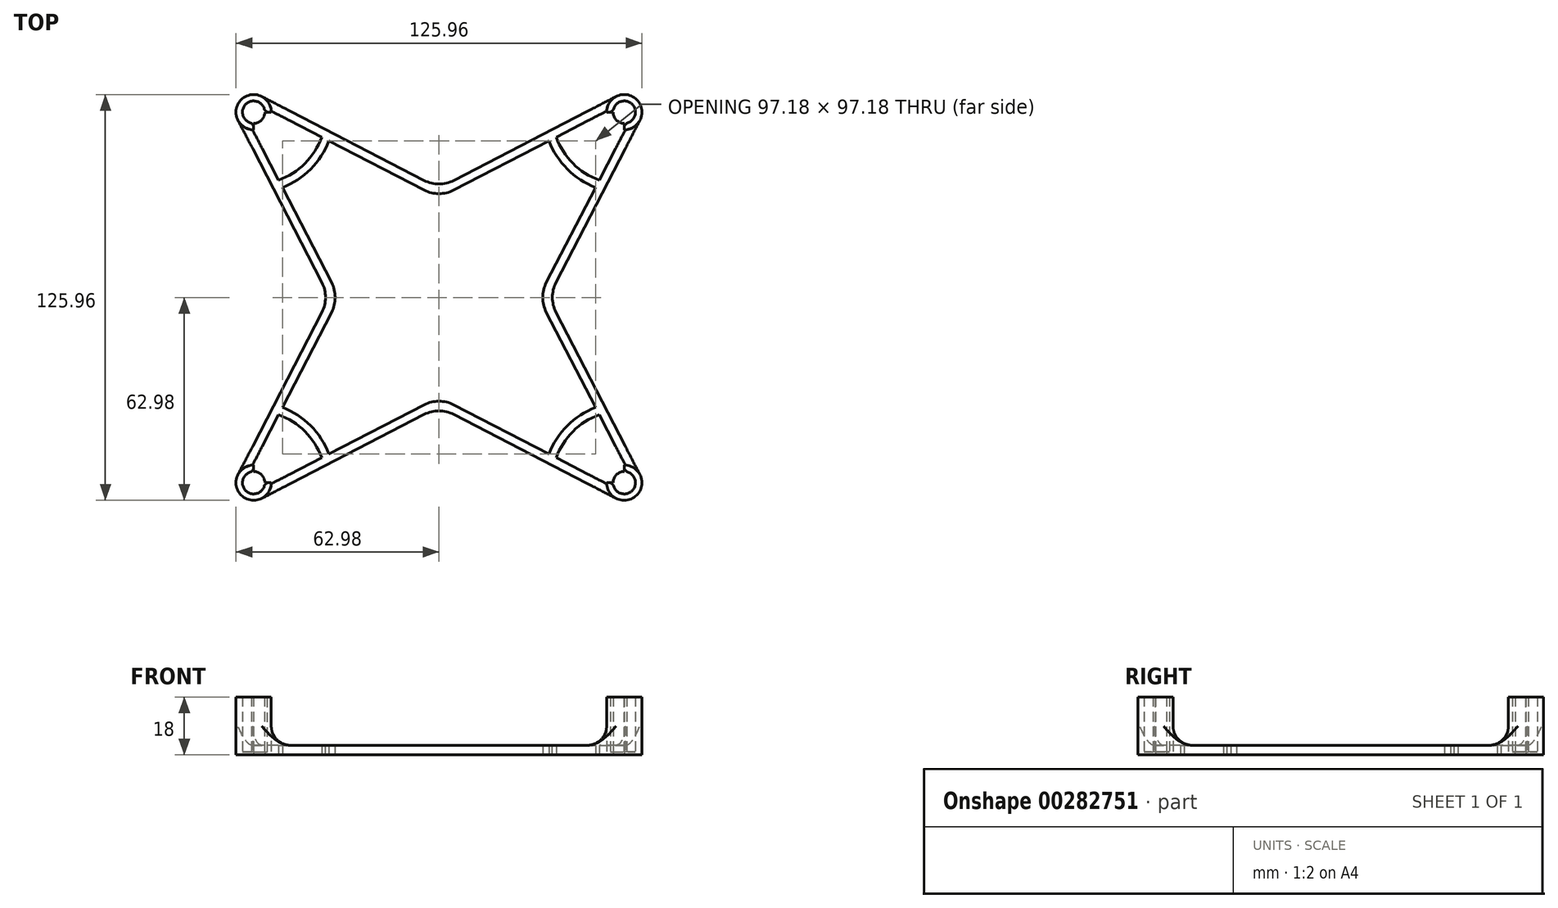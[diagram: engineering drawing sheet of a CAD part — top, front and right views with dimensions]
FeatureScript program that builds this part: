
annotation { "Feature Type Name" : "Feature", "Feature Type Description" : "" }
export const myFeature = defineFeature(function(context is Context, id is Id, definition is map)
    precondition{}
    {
        {
            var Q0;
            Q0=qCreatedBy(makeId("Top.planeOp"),FACE);
            var sketch = newSketch(context, id + "F0", { "sketchPlane" : qUnion([Q0])});
            skLineSegment(sketch, "E0.rect.bottom", {"start": v(57.5, 57.5) * mm, "end": v(-57.5, 57.5) * mm});
            skLineSegment(sketch, "E0.rect.top", {"start": v(57.5, -57.5) * mm, "end": v(-57.5, -57.5) * mm});
            skLineSegment(sketch, "E0.rect.left", {"start": v(57.5, 57.5) * mm, "end": v(57.5, -57.5) * mm});
            skLineSegment(sketch, "E0.rect.right", {"start": v(-57.5, 57.5) * mm, "end": v(-57.5, -57.5) * mm});
            skPoint(sketch, "E0.rect.middle", {"position": v(0, 0) * mm});
            skLineSegment(sketch, "E1", {"start": v(0, 33.94) * mm, "end": v(-33.94, 0) * mm});
            skLineSegment(sketch, "E2", {"start": v(-33.94, 0) * mm, "end": v(0, -33.94) * mm});
            skLineSegment(sketch, "E3", {"start": v(0, -33.94) * mm, "end": v(33.94, 0) * mm});
            skLineSegment(sketch, "E4", {"start": v(33.94, 0) * mm, "end": v(0, 33.94) * mm});
            skCircle(sketch, "E5", {"center": v(57.5, 57.5) * mm, "radius": 3.48 * mm});
            skCircle(sketch, "E6", {"center": v(57.5, 57.5) * mm, "radius": 5.47 * mm});
            skLineSegment(sketch, "E7", {"start": v(57.5, 60.98) * mm, "end": v(57.5, 62.98) * mm, "construction": true});
            skCircle(sketch, "E8", {"center": v(-57.5, 57.5) * mm, "radius": 3.48 * mm});
            skCircle(sketch, "E9", {"center": v(-57.5, 57.5) * mm, "radius": 5.47 * mm});
            skCircle(sketch, "E10", {"center": v(-57.5, -57.5) * mm, "radius": 3.48 * mm});
            skCircle(sketch, "E11", {"center": v(-57.5, -57.5) * mm, "radius": 5.47 * mm});
            skCircle(sketch, "E12", {"center": v(57.5, -57.5) * mm, "radius": 3.48 * mm});
            skCircle(sketch, "E13", {"center": v(57.5, -57.5) * mm, "radius": 5.47 * mm});
            skLineSegment(sketch, "E14", {"start": v(62.36, 54.99) * mm, "end": v(33.94, 0) * mm});
            skLineSegment(sketch, "E15", {"start": v(33.94, 0) * mm, "end": v(62.36, -54.99) * mm});
            skLineSegment(sketch, "E16", {"start": v(54.99, -62.36) * mm, "end": v(0, -33.94) * mm});
            skLineSegment(sketch, "E17", {"start": v(0, -33.94) * mm, "end": v(-54.99, -62.36) * mm});
            skLineSegment(sketch, "E18", {"start": v(-62.36, -54.99) * mm, "end": v(-33.94, 0) * mm});
            skLineSegment(sketch, "E19", {"start": v(-33.94, 0) * mm, "end": v(-62.36, 54.99) * mm});
            skLineSegment(sketch, "E20", {"start": v(-54.99, 62.36) * mm, "end": v(0, 33.94) * mm});
            skLineSegment(sketch, "E21", {"start": v(0, 33.94) * mm, "end": v(54.99, 62.36) * mm});
            skLineSegment(sketch, "E22.0", {"start": v(30.94, 0) * mm, "end": v(0, 30.94) * mm});
            skLineSegment(sketch, "E22.1", {"start": v(0, -30.94) * mm, "end": v(30.94, 0) * mm});
            skLineSegment(sketch, "E22.2", {"start": v(-30.94, 0) * mm, "end": v(0, -30.94) * mm});
            skLineSegment(sketch, "E22.3", {"start": v(0, 30.94) * mm, "end": v(-30.94, 0) * mm});
            skLineSegment(sketch, "E23", {"start": v(-30.94, 0) * mm, "end": v(-57.84, 52.04) * mm});
            skLineSegment(sketch, "E24", {"start": v(-30.94, 0) * mm, "end": v(-57.84, -52.04) * mm});
            skLineSegment(sketch, "E25", {"start": v(30.94, 0) * mm, "end": v(33.94, 0) * mm, "construction": true});
            skLineSegment(sketch, "E26", {"start": v(0, -30.94) * mm, "end": v(-52.04, -57.84) * mm});
            skLineSegment(sketch, "E27", {"start": v(0, -30.94) * mm, "end": v(52.04, -57.84) * mm});
            skLineSegment(sketch, "E28", {"start": v(57.84, -52.04) * mm, "end": v(30.94, 0) * mm});
            skLineSegment(sketch, "E29", {"start": v(30.94, 0) * mm, "end": v(57.84, 52.04) * mm});
            skLineSegment(sketch, "E30", {"start": v(52.04, 57.84) * mm, "end": v(0, 30.94) * mm});
            skLineSegment(sketch, "E31", {"start": v(0, 30.94) * mm, "end": v(-52.04, 57.84) * mm});
            skCircle(sketch, "E32", {"center": v(57.5, 57.5) * mm, "radius": 22.5 * mm});
            skCircle(sketch, "E33", {"center": v(57.5, 57.5) * mm, "radius": 25 * mm});
            skLineSegment(sketch, "E34", {"start": v(57.5, 80) * mm, "end": v(57.5, 82.5) * mm, "construction": true});
            skCircle(sketch, "E35", {"center": v(-57.5, 57.5) * mm, "radius": 22.5 * mm});
            skCircle(sketch, "E36", {"center": v(-57.5, 57.5) * mm, "radius": 25 * mm});
            skCircle(sketch, "E37", {"center": v(-57.5, -57.5) * mm, "radius": 22.5 * mm});
            skCircle(sketch, "E38", {"center": v(-57.5, -57.5) * mm, "radius": 25 * mm});
            skCircle(sketch, "E39", {"center": v(57.5, -57.5) * mm, "radius": 22.5 * mm});
            skCircle(sketch, "E40", {"center": v(57.5, -57.5) * mm, "radius": 25 * mm});
            skSolve(sketch);
        }
        {
            var Q0;
            {var subQ1=sQuery(id+"F0.wireOp",EDGE,"E23");var subQ5=sQuery(id+"F0.wireOp",EDGE,"E0.rect.right");var subQ6=makeQuery(id+"F0.imprint","INTERSECT",VERTEX,{"derivedFrom":[subQ5,subQ1]});Q0=makeQuery(id+"F0.imprint","IMPRINT",FACE,{"disambiguationData":[TD([[makeQuery(id+"F0.imprint","IMPRINT",EDGE,{"disambiguationData":[TD([[subQ6,-1.0]])],"derivedFrom":subQ5}),1.0]])]});}
            var Q1;
            {var subQ1=sQuery(id+"F0.wireOp",EDGE,"E0.rect.right");var subQ5=sQuery(id+"F0.wireOp",EDGE,"E23");var subQ6=makeQuery(id+"F0.imprint","INTERSECT",VERTEX,{"derivedFrom":[subQ1,subQ5]});Q1=makeQuery(id+"F0.imprint","IMPRINT",FACE,{"disambiguationData":[TD([[makeQuery(id+"F0.imprint","IMPRINT",EDGE,{"disambiguationData":[TD([[subQ6,-1.0]])],"derivedFrom":subQ1}),-1.0]])]});}
            var Q2;
            {var subQ0=sQuery(id+"F0.wireOp",EDGE,"E9");var subQ7=sQuery(id+"F0.wireOp",EDGE,"E0.rect.bottom");var subQ8=makeQuery(id+"F0.imprint","INTERSECT",VERTEX,{"derivedFrom":[subQ7,subQ0]});Q2=makeQuery(id+"F0.imprint","IMPRINT",FACE,{"disambiguationData":[TD([[makeQuery(id+"F0.imprint","IMPRINT",EDGE,{"disambiguationData":[TD([[subQ8,-1.0]])],"derivedFrom":subQ7}),-1.0]])]});}
            var Q3;
            {var subQ1=sQuery(id+"F0.wireOp",EDGE,"E0.rect.bottom");var subQ5=sQuery(id+"F0.wireOp",EDGE,"E20");var subQ6=makeQuery(id+"F0.imprint","INTERSECT",VERTEX,{"derivedFrom":[subQ1,subQ5]});Q3=makeQuery(id+"F0.imprint","IMPRINT",FACE,{"disambiguationData":[TD([[makeQuery(id+"F0.imprint","IMPRINT",EDGE,{"disambiguationData":[TD([[subQ6,-1.0]])],"derivedFrom":subQ1}),-1.0]])]});}
            var Q4;
            {var subQ3=sQuery(id+"F0.wireOp",EDGE,"E20");var subQ5=sQuery(id+"F0.wireOp",EDGE,"E0.rect.bottom");var subQ7=makeQuery(id+"F0.imprint","INTERSECT",VERTEX,{"derivedFrom":[subQ5,subQ3]});Q4=makeQuery(id+"F0.imprint","IMPRINT",FACE,{"disambiguationData":[TD([[makeQuery(id+"F0.imprint","IMPRINT",EDGE,{"disambiguationData":[TD([[subQ7,-1.0]])],"derivedFrom":subQ5}),1.0]])]});}
            var Q5;
            {var subQ0=sQuery(id+"F0.wireOp",EDGE,"E36");var subQ3=sQuery(id+"F0.wireOp",EDGE,"E19");var subQ4=makeQuery(id+"F0.imprint","INTERSECT",VERTEX,{"derivedFrom":[subQ3,subQ0]});Q5=makeQuery(id+"F0.imprint","IMPRINT",FACE,{"disambiguationData":[TD([[makeQuery(id+"F0.imprint","IMPRINT",EDGE,{"disambiguationData":[TD([[subQ4,-1.0]])],"derivedFrom":subQ3}),-1.0]])]});}
            var Q6;
            {var subQ1=sQuery(id+"F0.wireOp",EDGE,"E23");var subQ5=sQuery(id+"F0.wireOp",EDGE,"E1");var subQ6=makeQuery(id+"F0.imprint","INTERSECT",VERTEX,{"derivedFrom":[subQ5,subQ1]});Q6=makeQuery(id+"F0.imprint","IMPRINT",FACE,{"disambiguationData":[TD([[makeQuery(id+"F0.imprint","IMPRINT",EDGE,{"disambiguationData":[TD([[subQ6,-1.0]])],"derivedFrom":subQ1}),1.0]])]});}
            var Q7;
            {var subQ3=sQuery(id+"F0.wireOp",EDGE,"E20");var subQ5=sQuery(id+"F0.wireOp",EDGE,"E35");var subQ7=makeQuery(id+"F0.imprint","INTERSECT",VERTEX,{"derivedFrom":[subQ3,subQ5]});Q7=makeQuery(id+"F0.imprint","IMPRINT",FACE,{"disambiguationData":[TD([[makeQuery(id+"F0.imprint","IMPRINT",EDGE,{"disambiguationData":[TD([[subQ7,-1.0]])],"derivedFrom":subQ3}),-1.0]])]});}
            var Q8;
            {var subQ1=sQuery(id+"F0.wireOp",EDGE,"E31");var subQ5=sQuery(id+"F0.wireOp",EDGE,"E1");var subQ6=makeQuery(id+"F0.imprint","INTERSECT",VERTEX,{"derivedFrom":[subQ5,subQ1]});Q8=makeQuery(id+"F0.imprint","IMPRINT",FACE,{"disambiguationData":[TD([[makeQuery(id+"F0.imprint","IMPRINT",EDGE,{"disambiguationData":[TD([[subQ6,-1.0]])],"derivedFrom":subQ1}),-1.0]])]});}
            var Q9;
            {var subQ0=sQuery(id+"F0.wireOp",EDGE,"E31");var subQ1=sQuery(id+"F0.wireOp",EDGE,"E1");var subQ2=makeQuery(id+"F0.imprint","INTERSECT",VERTEX,{"derivedFrom":[subQ1,subQ0]});Q9=makeQuery(id+"F0.imprint","IMPRINT",FACE,{"disambiguationData":[TD([[makeQuery(id+"F0.imprint","IMPRINT",EDGE,{"disambiguationData":[TD([[subQ2,1.0]])],"derivedFrom":subQ1}),1.0]])]});}
            var Q10;
            {var subQ1=sQuery(id+"F0.wireOp",EDGE,"E30");var subQ5=sQuery(id+"F0.wireOp",EDGE,"E4");var subQ6=makeQuery(id+"F0.imprint","INTERSECT",VERTEX,{"derivedFrom":[subQ5,subQ1]});Q10=makeQuery(id+"F0.imprint","IMPRINT",FACE,{"disambiguationData":[TD([[makeQuery(id+"F0.imprint","IMPRINT",EDGE,{"disambiguationData":[TD([[subQ6,1.0]])],"derivedFrom":subQ1}),-1.0]])]});}
            var Q11;
            {var subQ0=sQuery(id+"F0.wireOp",EDGE,"E33");var subQ3=sQuery(id+"F0.wireOp",EDGE,"E21");var subQ4=makeQuery(id+"F0.imprint","INTERSECT",VERTEX,{"derivedFrom":[subQ3,subQ0]});Q11=makeQuery(id+"F0.imprint","IMPRINT",FACE,{"disambiguationData":[TD([[makeQuery(id+"F0.imprint","IMPRINT",EDGE,{"disambiguationData":[TD([[subQ4,-1.0]])],"derivedFrom":subQ3}),-1.0]])]});}
            var Q12;
            {var subQ1=sQuery(id+"F0.wireOp",EDGE,"E30");var subQ5=sQuery(id+"F0.wireOp",EDGE,"E0.rect.bottom");var subQ6=makeQuery(id+"F0.imprint","INTERSECT",VERTEX,{"derivedFrom":[subQ5,subQ1]});Q12=makeQuery(id+"F0.imprint","IMPRINT",FACE,{"disambiguationData":[TD([[makeQuery(id+"F0.imprint","IMPRINT",EDGE,{"disambiguationData":[TD([[subQ6,-1.0]])],"derivedFrom":subQ5}),1.0]])]});}
            var Q13;
            {var subQ0=sQuery(id+"F0.wireOp",EDGE,"E30");var subQ1=sQuery(id+"F0.wireOp",EDGE,"E0.rect.bottom");var subQ2=makeQuery(id+"F0.imprint","INTERSECT",VERTEX,{"derivedFrom":[subQ1,subQ0]});Q13=makeQuery(id+"F0.imprint","IMPRINT",FACE,{"disambiguationData":[TD([[makeQuery(id+"F0.imprint","IMPRINT",EDGE,{"disambiguationData":[TD([[subQ2,-1.0]])],"derivedFrom":subQ1}),-1.0]])]});}
            var Q14;
            {var subQ7=sQuery(id+"F0.wireOp",EDGE,"E5");var subQ9=sQuery(id+"F0.wireOp",EDGE,"E0.rect.bottom");var subQ10=makeQuery(id+"F0.imprint","INTERSECT",VERTEX,{"derivedFrom":[subQ9,subQ7]});Q14=makeQuery(id+"F0.imprint","IMPRINT",FACE,{"disambiguationData":[TD([[makeQuery(id+"F0.imprint","IMPRINT",EDGE,{"disambiguationData":[TD([[subQ10,-1.0]])],"derivedFrom":subQ9}),-1.0]])]});}
            var Q15;
            {var subQ0=sQuery(id+"F0.wireOp",EDGE,"E29");var subQ1=sQuery(id+"F0.wireOp",EDGE,"E0.rect.left");var subQ2=makeQuery(id+"F0.imprint","INTERSECT",VERTEX,{"derivedFrom":[subQ1,subQ0]});Q15=makeQuery(id+"F0.imprint","IMPRINT",FACE,{"disambiguationData":[TD([[makeQuery(id+"F0.imprint","IMPRINT",EDGE,{"disambiguationData":[TD([[subQ2,-1.0]])],"derivedFrom":subQ1}),1.0]])]});}
            var Q16;
            {var subQ1=sQuery(id+"F0.wireOp",EDGE,"E29");var subQ5=sQuery(id+"F0.wireOp",EDGE,"E0.rect.left");var subQ6=makeQuery(id+"F0.imprint","INTERSECT",VERTEX,{"derivedFrom":[subQ5,subQ1]});Q16=makeQuery(id+"F0.imprint","IMPRINT",FACE,{"disambiguationData":[TD([[makeQuery(id+"F0.imprint","IMPRINT",EDGE,{"disambiguationData":[TD([[subQ6,-1.0]])],"derivedFrom":subQ5}),-1.0]])]});}
            var Q17;
            {var subQ3=sQuery(id+"F0.wireOp",EDGE,"E14");var subQ5=sQuery(id+"F0.wireOp",EDGE,"E32");var subQ7=makeQuery(id+"F0.imprint","INTERSECT",VERTEX,{"derivedFrom":[subQ3,subQ5]});Q17=makeQuery(id+"F0.imprint","IMPRINT",FACE,{"disambiguationData":[TD([[makeQuery(id+"F0.imprint","IMPRINT",EDGE,{"disambiguationData":[TD([[subQ7,-1.0]])],"derivedFrom":subQ3}),-1.0]])]});}
            var Q18;
            {var subQ1=sQuery(id+"F0.wireOp",EDGE,"E29");var subQ5=sQuery(id+"F0.wireOp",EDGE,"E4");var subQ6=makeQuery(id+"F0.imprint","INTERSECT",VERTEX,{"derivedFrom":[subQ5,subQ1]});Q18=makeQuery(id+"F0.imprint","IMPRINT",FACE,{"disambiguationData":[TD([[makeQuery(id+"F0.imprint","IMPRINT",EDGE,{"disambiguationData":[TD([[subQ6,-1.0]])],"derivedFrom":subQ1}),-1.0]])]});}
            var Q19;
            {var subQ3=sQuery(id+"F0.wireOp",EDGE,"E28");var subQ5=sQuery(id+"F0.wireOp",EDGE,"E3");var subQ6=makeQuery(id+"F0.imprint","INTERSECT",VERTEX,{"derivedFrom":[subQ5,subQ3]});Q19=makeQuery(id+"F0.imprint","IMPRINT",FACE,{"disambiguationData":[TD([[makeQuery(id+"F0.imprint","IMPRINT",EDGE,{"disambiguationData":[TD([[subQ6,-1.0]])],"derivedFrom":subQ5}),1.0]])]});}
            var Q20;
            {var subQ3=sQuery(id+"F0.wireOp",EDGE,"E23");var subQ5=sQuery(id+"F0.wireOp",EDGE,"E1");var subQ6=makeQuery(id+"F0.imprint","INTERSECT",VERTEX,{"derivedFrom":[subQ5,subQ3]});Q20=makeQuery(id+"F0.imprint","IMPRINT",FACE,{"disambiguationData":[TD([[makeQuery(id+"F0.imprint","IMPRINT",EDGE,{"disambiguationData":[TD([[subQ6,-1.0]])],"derivedFrom":subQ5}),1.0]])]});}
            var Q21;
            {var subQ1=sQuery(id+"F0.wireOp",EDGE,"E24");var subQ5=sQuery(id+"F0.wireOp",EDGE,"E2");var subQ6=makeQuery(id+"F0.imprint","INTERSECT",VERTEX,{"derivedFrom":[subQ5,subQ1]});Q21=makeQuery(id+"F0.imprint","IMPRINT",FACE,{"disambiguationData":[TD([[makeQuery(id+"F0.imprint","IMPRINT",EDGE,{"disambiguationData":[TD([[subQ6,-1.0]])],"derivedFrom":subQ1}),-1.0]])]});}
            var Q22;
            {var subQ1=sQuery(id+"F0.wireOp",EDGE,"E28");var subQ5=sQuery(id+"F0.wireOp",EDGE,"E3");var subQ6=makeQuery(id+"F0.imprint","INTERSECT",VERTEX,{"derivedFrom":[subQ5,subQ1]});Q22=makeQuery(id+"F0.imprint","IMPRINT",FACE,{"disambiguationData":[TD([[makeQuery(id+"F0.imprint","IMPRINT",EDGE,{"disambiguationData":[TD([[subQ6,1.0]])],"derivedFrom":subQ1}),-1.0]])]});}
            var Q23;
            {var subQ0=sQuery(id+"F0.wireOp",EDGE,"E40");var subQ3=sQuery(id+"F0.wireOp",EDGE,"E15");var subQ4=makeQuery(id+"F0.imprint","INTERSECT",VERTEX,{"derivedFrom":[subQ3,subQ0]});Q23=makeQuery(id+"F0.imprint","IMPRINT",FACE,{"disambiguationData":[TD([[makeQuery(id+"F0.imprint","IMPRINT",EDGE,{"disambiguationData":[TD([[subQ4,-1.0]])],"derivedFrom":subQ3}),-1.0]])]});}
            var Q24;
            {var subQ3=sQuery(id+"F0.wireOp",EDGE,"E18");var subQ5=sQuery(id+"F0.wireOp",EDGE,"E37");var subQ7=makeQuery(id+"F0.imprint","INTERSECT",VERTEX,{"derivedFrom":[subQ3,subQ5]});Q24=makeQuery(id+"F0.imprint","IMPRINT",FACE,{"disambiguationData":[TD([[makeQuery(id+"F0.imprint","IMPRINT",EDGE,{"disambiguationData":[TD([[subQ7,-1.0]])],"derivedFrom":subQ3}),-1.0]])]});}
            var Q25;
            {var subQ3=sQuery(id+"F0.wireOp",EDGE,"E18");var subQ5=sQuery(id+"F0.wireOp",EDGE,"E0.rect.right");var subQ7=makeQuery(id+"F0.imprint","INTERSECT",VERTEX,{"derivedFrom":[subQ5,subQ3]});Q25=makeQuery(id+"F0.imprint","IMPRINT",FACE,{"disambiguationData":[TD([[makeQuery(id+"F0.imprint","IMPRINT",EDGE,{"disambiguationData":[TD([[subQ7,-1.0]])],"derivedFrom":subQ5}),1.0]])]});}
            var Q26;
            {var subQ1=sQuery(id+"F0.wireOp",EDGE,"E0.rect.right");var subQ5=sQuery(id+"F0.wireOp",EDGE,"E18");var subQ6=makeQuery(id+"F0.imprint","INTERSECT",VERTEX,{"derivedFrom":[subQ1,subQ5]});Q26=makeQuery(id+"F0.imprint","IMPRINT",FACE,{"disambiguationData":[TD([[makeQuery(id+"F0.imprint","IMPRINT",EDGE,{"disambiguationData":[TD([[subQ6,-1.0]])],"derivedFrom":subQ1}),-1.0]])]});}
            var Q27;
            {var subQ0=sQuery(id+"F0.wireOp",EDGE,"E11");var subQ1=sQuery(id+"F0.wireOp",EDGE,"E0.rect.top");var subQ2=makeQuery(id+"F0.imprint","INTERSECT",VERTEX,{"derivedFrom":[subQ1,subQ0]});Q27=makeQuery(id+"F0.imprint","IMPRINT",FACE,{"disambiguationData":[TD([[makeQuery(id+"F0.imprint","IMPRINT",EDGE,{"disambiguationData":[TD([[subQ2,-1.0]])],"derivedFrom":subQ1}),1.0]])]});}
            var Q28;
            {var subQ1=sQuery(id+"F0.wireOp",EDGE,"E0.rect.top");var subQ5=sQuery(id+"F0.wireOp",EDGE,"E17");var subQ6=makeQuery(id+"F0.imprint","INTERSECT",VERTEX,{"derivedFrom":[subQ1,subQ5]});Q28=makeQuery(id+"F0.imprint","IMPRINT",FACE,{"disambiguationData":[TD([[makeQuery(id+"F0.imprint","IMPRINT",EDGE,{"disambiguationData":[TD([[subQ6,-1.0]])],"derivedFrom":subQ1}),1.0]])]});}
            var Q29;
            {var subQ3=sQuery(id+"F0.wireOp",EDGE,"E17");var subQ5=sQuery(id+"F0.wireOp",EDGE,"E0.rect.top");var subQ7=makeQuery(id+"F0.imprint","INTERSECT",VERTEX,{"derivedFrom":[subQ5,subQ3]});Q29=makeQuery(id+"F0.imprint","IMPRINT",FACE,{"disambiguationData":[TD([[makeQuery(id+"F0.imprint","IMPRINT",EDGE,{"disambiguationData":[TD([[subQ7,-1.0]])],"derivedFrom":subQ5}),-1.0]])]});}
            var Q30;
            {var subQ0=sQuery(id+"F0.wireOp",EDGE,"E38");var subQ3=sQuery(id+"F0.wireOp",EDGE,"E17");var subQ4=makeQuery(id+"F0.imprint","INTERSECT",VERTEX,{"derivedFrom":[subQ3,subQ0]});Q30=makeQuery(id+"F0.imprint","IMPRINT",FACE,{"disambiguationData":[TD([[makeQuery(id+"F0.imprint","IMPRINT",EDGE,{"disambiguationData":[TD([[subQ4,-1.0]])],"derivedFrom":subQ3}),-1.0]])]});}
            var Q31;
            {var subQ1=sQuery(id+"F0.wireOp",EDGE,"E26");var subQ5=sQuery(id+"F0.wireOp",EDGE,"E2");var subQ6=makeQuery(id+"F0.imprint","INTERSECT",VERTEX,{"derivedFrom":[subQ5,subQ1]});Q31=makeQuery(id+"F0.imprint","IMPRINT",FACE,{"disambiguationData":[TD([[makeQuery(id+"F0.imprint","IMPRINT",EDGE,{"disambiguationData":[TD([[subQ6,-1.0]])],"derivedFrom":subQ1}),1.0]])]});}
            var Q32;
            {var subQ3=sQuery(id+"F0.wireOp",EDGE,"E26");var subQ5=sQuery(id+"F0.wireOp",EDGE,"E2");var subQ6=makeQuery(id+"F0.imprint","INTERSECT",VERTEX,{"derivedFrom":[subQ5,subQ3]});Q32=makeQuery(id+"F0.imprint","IMPRINT",FACE,{"disambiguationData":[TD([[makeQuery(id+"F0.imprint","IMPRINT",EDGE,{"disambiguationData":[TD([[subQ6,-1.0]])],"derivedFrom":subQ5}),1.0]])]});}
            var Q33;
            {var subQ1=sQuery(id+"F0.wireOp",EDGE,"E27");var subQ5=sQuery(id+"F0.wireOp",EDGE,"E3");var subQ6=makeQuery(id+"F0.imprint","INTERSECT",VERTEX,{"derivedFrom":[subQ5,subQ1]});Q33=makeQuery(id+"F0.imprint","IMPRINT",FACE,{"disambiguationData":[TD([[makeQuery(id+"F0.imprint","IMPRINT",EDGE,{"disambiguationData":[TD([[subQ6,-1.0]])],"derivedFrom":subQ1}),-1.0]])]});}
            var Q34;
            {var subQ3=sQuery(id+"F0.wireOp",EDGE,"E16");var subQ5=sQuery(id+"F0.wireOp",EDGE,"E39");var subQ7=makeQuery(id+"F0.imprint","INTERSECT",VERTEX,{"derivedFrom":[subQ3,subQ5]});Q34=makeQuery(id+"F0.imprint","IMPRINT",FACE,{"disambiguationData":[TD([[makeQuery(id+"F0.imprint","IMPRINT",EDGE,{"disambiguationData":[TD([[subQ7,-1.0]])],"derivedFrom":subQ3}),-1.0]])]});}
            var Q35;
            {var subQ3=sQuery(id+"F0.wireOp",EDGE,"E0.rect.top");var subQ9=sQuery(id+"F0.wireOp",EDGE,"E12");var subQ11=makeQuery(id+"F0.imprint","INTERSECT",VERTEX,{"derivedFrom":[subQ3,subQ9]});Q35=makeQuery(id+"F0.imprint","IMPRINT",FACE,{"disambiguationData":[TD([[makeQuery(id+"F0.imprint","IMPRINT",EDGE,{"disambiguationData":[TD([[subQ11,-1.0]])],"derivedFrom":subQ3}),1.0]])]});}
            var Q36;
            {var subQ1=sQuery(id+"F0.wireOp",EDGE,"E0.rect.top");var subQ5=sQuery(id+"F0.wireOp",EDGE,"E27");var subQ6=makeQuery(id+"F0.imprint","INTERSECT",VERTEX,{"derivedFrom":[subQ1,subQ5]});Q36=makeQuery(id+"F0.imprint","IMPRINT",FACE,{"disambiguationData":[TD([[makeQuery(id+"F0.imprint","IMPRINT",EDGE,{"disambiguationData":[TD([[subQ6,-1.0]])],"derivedFrom":subQ1}),1.0]])]});}
            var Q37;
            {var subQ1=sQuery(id+"F0.wireOp",EDGE,"E27");var subQ5=sQuery(id+"F0.wireOp",EDGE,"E0.rect.top");var subQ6=makeQuery(id+"F0.imprint","INTERSECT",VERTEX,{"derivedFrom":[subQ5,subQ1]});Q37=makeQuery(id+"F0.imprint","IMPRINT",FACE,{"disambiguationData":[TD([[makeQuery(id+"F0.imprint","IMPRINT",EDGE,{"disambiguationData":[TD([[subQ6,-1.0]])],"derivedFrom":subQ5}),-1.0]])]});}
            var Q38;
            {var subQ1=sQuery(id+"F0.wireOp",EDGE,"E0.rect.left");var subQ5=sQuery(id+"F0.wireOp",EDGE,"E15");var subQ6=makeQuery(id+"F0.imprint","INTERSECT",VERTEX,{"derivedFrom":[subQ1,subQ5]});Q38=makeQuery(id+"F0.imprint","IMPRINT",FACE,{"disambiguationData":[TD([[makeQuery(id+"F0.imprint","IMPRINT",EDGE,{"disambiguationData":[TD([[subQ6,-1.0]])],"derivedFrom":subQ1}),1.0]])]});}
            var Q39;
            {var subQ3=sQuery(id+"F0.wireOp",EDGE,"E15");var subQ5=sQuery(id+"F0.wireOp",EDGE,"E0.rect.left");var subQ7=makeQuery(id+"F0.imprint","INTERSECT",VERTEX,{"derivedFrom":[subQ5,subQ3]});Q39=makeQuery(id+"F0.imprint","IMPRINT",FACE,{"disambiguationData":[TD([[makeQuery(id+"F0.imprint","IMPRINT",EDGE,{"disambiguationData":[TD([[subQ7,-1.0]])],"derivedFrom":subQ5}),-1.0]])]});}
            var Q40;
            {var subQ3=sQuery(id+"F0.wireOp",EDGE,"E23");var subQ5=sQuery(id+"F0.wireOp",EDGE,"E36");var subQ7=makeQuery(id+"F0.imprint","INTERSECT",VERTEX,{"derivedFrom":[subQ3,subQ5]});Q40=makeQuery(id+"F0.imprint","IMPRINT",FACE,{"disambiguationData":[TD([[makeQuery(id+"F0.imprint","IMPRINT",EDGE,{"disambiguationData":[TD([[subQ7,-1.0]])],"derivedFrom":subQ3}),-1.0]])]});}
            var Q41;
            {var subQ0=sQuery(id+"F0.wireOp",EDGE,"E33");var subQ3=sQuery(id+"F0.wireOp",EDGE,"E29");var subQ4=makeQuery(id+"F0.imprint","INTERSECT",VERTEX,{"derivedFrom":[subQ3,subQ0]});Q41=makeQuery(id+"F0.imprint","IMPRINT",FACE,{"disambiguationData":[TD([[makeQuery(id+"F0.imprint","IMPRINT",EDGE,{"disambiguationData":[TD([[subQ4,-1.0]])],"derivedFrom":subQ3}),1.0]])]});}
            var Q42;
            {var subQ0=sQuery(id+"F0.wireOp",EDGE,"E40");var subQ3=sQuery(id+"F0.wireOp",EDGE,"E27");var subQ4=makeQuery(id+"F0.imprint","INTERSECT",VERTEX,{"derivedFrom":[subQ3,subQ0]});Q42=makeQuery(id+"F0.imprint","IMPRINT",FACE,{"disambiguationData":[TD([[makeQuery(id+"F0.imprint","IMPRINT",EDGE,{"disambiguationData":[TD([[subQ4,-1.0]])],"derivedFrom":subQ3}),1.0]])]});}
            var Q43;
            {var subQ0=sQuery(id+"F0.wireOp",EDGE,"E38");var subQ3=sQuery(id+"F0.wireOp",EDGE,"E24");var subQ4=makeQuery(id+"F0.imprint","INTERSECT",VERTEX,{"derivedFrom":[subQ3,subQ0]});Q43=makeQuery(id+"F0.imprint","IMPRINT",FACE,{"disambiguationData":[TD([[makeQuery(id+"F0.imprint","IMPRINT",EDGE,{"disambiguationData":[TD([[subQ4,-1.0]])],"derivedFrom":subQ3}),1.0]])]});}
            extrude(context, id + "F1", {"entities" : qUnion([Q0, Q1, Q2, Q3, Q4, Q5, Q6, Q7, Q8, Q9, Q10, Q11, Q12, Q13, Q14, Q15, Q16, Q17, Q18, Q19, Q20, Q21, Q22, Q23, Q24, Q25, Q26, Q27, Q28, Q29, Q30, Q31, Q32, Q33, Q34, Q35, Q36, Q37, Q38, Q39, Q40, Q41, Q42, Q43]), "depth" : 3 * mm});
        }
        {
            var Q0;
            {var subQ0=sQuery(id+"F0.wireOp",EDGE,"E11");var subQ1=sQuery(id+"F0.wireOp",EDGE,"E0.rect.top");var subQ2=makeQuery(id+"F0.imprint","INTERSECT",VERTEX,{"derivedFrom":[subQ1,subQ0]});Q0=makeQuery(id+"F0.imprint","IMPRINT",FACE,{"disambiguationData":[TD([[makeQuery(id+"F0.imprint","IMPRINT",EDGE,{"disambiguationData":[TD([[subQ2,-1.0]])],"derivedFrom":subQ1}),1.0]])]});}
            var Q1;
            {var subQ0=sQuery(id+"F0.wireOp",EDGE,"E9");var subQ7=sQuery(id+"F0.wireOp",EDGE,"E0.rect.bottom");var subQ8=makeQuery(id+"F0.imprint","INTERSECT",VERTEX,{"derivedFrom":[subQ7,subQ0]});Q1=makeQuery(id+"F0.imprint","IMPRINT",FACE,{"disambiguationData":[TD([[makeQuery(id+"F0.imprint","IMPRINT",EDGE,{"disambiguationData":[TD([[subQ8,-1.0]])],"derivedFrom":subQ7}),-1.0]])]});}
            var Q2;
            {var subQ3=sQuery(id+"F0.wireOp",EDGE,"E0.rect.top");var subQ9=sQuery(id+"F0.wireOp",EDGE,"E12");var subQ11=makeQuery(id+"F0.imprint","INTERSECT",VERTEX,{"derivedFrom":[subQ3,subQ9]});Q2=makeQuery(id+"F0.imprint","IMPRINT",FACE,{"disambiguationData":[TD([[makeQuery(id+"F0.imprint","IMPRINT",EDGE,{"disambiguationData":[TD([[subQ11,-1.0]])],"derivedFrom":subQ3}),1.0]])]});}
            var Q3;
            {var subQ7=sQuery(id+"F0.wireOp",EDGE,"E5");var subQ9=sQuery(id+"F0.wireOp",EDGE,"E0.rect.bottom");var subQ10=makeQuery(id+"F0.imprint","INTERSECT",VERTEX,{"derivedFrom":[subQ9,subQ7]});Q3=makeQuery(id+"F0.imprint","IMPRINT",FACE,{"disambiguationData":[TD([[makeQuery(id+"F0.imprint","IMPRINT",EDGE,{"disambiguationData":[TD([[subQ10,-1.0]])],"derivedFrom":subQ9}),-1.0]])]});}
            extrude(context, id + "F2", {"entities" : qUnion([Q0, Q1, Q2, Q3]), "operationType" : NewBodyOperationType.ADD, "depth" : 18 * mm});
        }
        {
            var Q0;
            {var subQ1=sQuery(id+"F0.wireOp",EDGE,"E0.rect.right");var subQ3=sQuery(id+"F0.wireOp",EDGE,"E0.rect.bottom");var subQ5=makeQuery(id+"F0.imprint","INTERSECT",VERTEX,{"derivedFrom":[subQ3,subQ1]});Q0=makeQuery(id+"F0.imprint","IMPRINT",FACE,{"disambiguationData":[TD([[makeQuery(id+"F0.imprint","IMPRINT",EDGE,{"disambiguationData":[TD([[subQ5,1.0]])],"derivedFrom":subQ3}),-1.0]])]});}
            var Q1;
            {var subQ1=sQuery(id+"F0.wireOp",EDGE,"E0.rect.left");var subQ3=sQuery(id+"F0.wireOp",EDGE,"E0.rect.bottom");var subQ5=makeQuery(id+"F0.imprint","INTERSECT",VERTEX,{"derivedFrom":[subQ3,subQ1]});Q1=makeQuery(id+"F0.imprint","IMPRINT",FACE,{"disambiguationData":[TD([[makeQuery(id+"F0.imprint","IMPRINT",EDGE,{"disambiguationData":[TD([[subQ5,-1.0]])],"derivedFrom":subQ3}),-1.0]])]});}
            var Q2;
            {var subQ1=sQuery(id+"F0.wireOp",EDGE,"E0.rect.left");var subQ3=sQuery(id+"F0.wireOp",EDGE,"E0.rect.top");var subQ5=makeQuery(id+"F0.imprint","INTERSECT",VERTEX,{"derivedFrom":[subQ3,subQ1]});Q2=makeQuery(id+"F0.imprint","IMPRINT",FACE,{"disambiguationData":[TD([[makeQuery(id+"F0.imprint","IMPRINT",EDGE,{"disambiguationData":[TD([[subQ5,-1.0]])],"derivedFrom":subQ3}),1.0]])]});}
            var Q3;
            {var subQ1=sQuery(id+"F0.wireOp",EDGE,"E0.rect.right");var subQ3=sQuery(id+"F0.wireOp",EDGE,"E0.rect.top");var subQ5=makeQuery(id+"F0.imprint","INTERSECT",VERTEX,{"derivedFrom":[subQ3,subQ1]});Q3=makeQuery(id+"F0.imprint","IMPRINT",FACE,{"disambiguationData":[TD([[makeQuery(id+"F0.imprint","IMPRINT",EDGE,{"disambiguationData":[TD([[subQ5,1.0]])],"derivedFrom":subQ3}),1.0]])]});}
            var Q4;
            {var subQ1=sQuery(id+"F0.wireOp",EDGE,"E0.rect.right");var subQ3=sQuery(id+"F0.wireOp",EDGE,"E0.rect.bottom");var subQ5=makeQuery(id+"F0.imprint","INTERSECT",VERTEX,{"derivedFrom":[subQ3,subQ1]});Q4=makeQuery(id+"F0.imprint","IMPRINT",FACE,{"disambiguationData":[TD([[makeQuery(id+"F0.imprint","IMPRINT",EDGE,{"disambiguationData":[TD([[subQ5,1.0]])],"derivedFrom":subQ3}),1.0]])]});}
            var Q5;
            {var subQ1=sQuery(id+"F0.wireOp",EDGE,"E0.rect.left");var subQ3=sQuery(id+"F0.wireOp",EDGE,"E0.rect.bottom");var subQ5=makeQuery(id+"F0.imprint","INTERSECT",VERTEX,{"derivedFrom":[subQ3,subQ1]});Q5=makeQuery(id+"F0.imprint","IMPRINT",FACE,{"disambiguationData":[TD([[makeQuery(id+"F0.imprint","IMPRINT",EDGE,{"disambiguationData":[TD([[subQ5,-1.0]])],"derivedFrom":subQ3}),1.0]])]});}
            var Q6;
            {var subQ1=sQuery(id+"F0.wireOp",EDGE,"E0.rect.left");var subQ3=sQuery(id+"F0.wireOp",EDGE,"E0.rect.top");var subQ5=makeQuery(id+"F0.imprint","INTERSECT",VERTEX,{"derivedFrom":[subQ3,subQ1]});Q6=makeQuery(id+"F0.imprint","IMPRINT",FACE,{"disambiguationData":[TD([[makeQuery(id+"F0.imprint","IMPRINT",EDGE,{"disambiguationData":[TD([[subQ5,-1.0]])],"derivedFrom":subQ3}),-1.0]])]});}
            var Q7;
            {var subQ1=sQuery(id+"F0.wireOp",EDGE,"E0.rect.right");var subQ3=sQuery(id+"F0.wireOp",EDGE,"E0.rect.top");var subQ5=makeQuery(id+"F0.imprint","INTERSECT",VERTEX,{"derivedFrom":[subQ3,subQ1]});Q7=makeQuery(id+"F0.imprint","IMPRINT",FACE,{"disambiguationData":[TD([[makeQuery(id+"F0.imprint","IMPRINT",EDGE,{"disambiguationData":[TD([[subQ5,1.0]])],"derivedFrom":subQ3}),-1.0]])]});}
            extrude(context, id + "F3", {"entities" : qUnion([Q0, Q1, Q2, Q3, Q4, Q5, Q6, Q7]), "operationType" : NewBodyOperationType.ADD, "depth" : 1 * mm});
        }
        {
            var Q0;
            Q0=makeQuery(id+"F1.opExtrude","SWEPT_EDGE",EDGE,{"disambiguationData":[OSD([sQuery(id+"F0.wireOp",EDGE,"E22.2"),sQuery(id+"F0.wireOp",EDGE,"E22.3"),sQuery(id+"F0.wireOp",EDGE,"E23"),sQuery(id+"F0.wireOp",EDGE,"E24")])]});
            var Q1;
            Q1=makeQuery(id+"F1.opExtrude","SWEPT_EDGE",EDGE,{"disambiguationData":[OSD([sQuery(id+"F0.wireOp",EDGE,"E1"),sQuery(id+"F0.wireOp",EDGE,"E2"),sQuery(id+"F0.wireOp",EDGE,"E18"),sQuery(id+"F0.wireOp",EDGE,"E19")])]});
            var Q2;
            Q2=makeQuery(id+"F1.opExtrude","SWEPT_EDGE",EDGE,{"disambiguationData":[OSD([sQuery(id+"F0.wireOp",EDGE,"E22.0"),sQuery(id+"F0.wireOp",EDGE,"E22.3"),sQuery(id+"F0.wireOp",EDGE,"E30"),sQuery(id+"F0.wireOp",EDGE,"E31")])]});
            var Q3;
            Q3=makeQuery(id+"F1.opExtrude","SWEPT_EDGE",EDGE,{"disambiguationData":[OSD([sQuery(id+"F0.wireOp",EDGE,"E1"),sQuery(id+"F0.wireOp",EDGE,"E4"),sQuery(id+"F0.wireOp",EDGE,"E20"),sQuery(id+"F0.wireOp",EDGE,"E21")])]});
            var Q4;
            Q4=makeQuery(id+"F1.opExtrude","SWEPT_EDGE",EDGE,{"disambiguationData":[OSD([sQuery(id+"F0.wireOp",EDGE,"E22.0"),sQuery(id+"F0.wireOp",EDGE,"E22.1"),sQuery(id+"F0.wireOp",EDGE,"E28"),sQuery(id+"F0.wireOp",EDGE,"E29")])]});
            var Q5;
            Q5=makeQuery(id+"F1.opExtrude","SWEPT_EDGE",EDGE,{"disambiguationData":[OSD([sQuery(id+"F0.wireOp",EDGE,"E3"),sQuery(id+"F0.wireOp",EDGE,"E4"),sQuery(id+"F0.wireOp",EDGE,"E14"),sQuery(id+"F0.wireOp",EDGE,"E15")])]});
            var Q6;
            Q6=makeQuery(id+"F1.opExtrude","SWEPT_EDGE",EDGE,{"disambiguationData":[OSD([sQuery(id+"F0.wireOp",EDGE,"E22.1"),sQuery(id+"F0.wireOp",EDGE,"E22.2"),sQuery(id+"F0.wireOp",EDGE,"E26"),sQuery(id+"F0.wireOp",EDGE,"E27")])]});
            var Q7;
            Q7=makeQuery(id+"F1.opExtrude","SWEPT_EDGE",EDGE,{"disambiguationData":[OSD([sQuery(id+"F0.wireOp",EDGE,"E2"),sQuery(id+"F0.wireOp",EDGE,"E3"),sQuery(id+"F0.wireOp",EDGE,"E16"),sQuery(id+"F0.wireOp",EDGE,"E17")])]});
            fillet(context, id + "F4", {"entities" : qUnion([Q0, Q1, Q2, Q3, Q4, Q5, Q6, Q7]), "radius" : 10 * mm, "tangentPropagation" : true, "allowEdgeOverflow" : false});
        }
        {
            var Q0;
            {var subQ0=sQuery(id+"F0.wireOp",EDGE,"E0.rect.bottom");var subQ1=sQuery(id+"F0.wireOp",EDGE,"E8");Q0=makeQuery(id+"F3.boolean.opBoolean","SPLIT",EDGE,{"disambiguationData":[topologyDisambiguationEdgeConnected([makeQuery(id+"F1.opExtrude","SWEPT_FACE",FACE,{"disambiguationData":[OSD([subQ1])]})])],"derivedFrom":makeQuery(id+"F2.boolean.opBoolean","MERGE",EDGE,{"derivedFrom":[makeQuery(id+"F1.opExtrude","SWEPT_EDGE",EDGE,{"disambiguationData":[OSD([subQ0,subQ1])]}),makeQuery(id+"F2.opExtrude","SWEPT_EDGE",EDGE,{"disambiguationData":[OSD([subQ0,subQ1])]})]})});}
            var Q1;
            {var subQ0=sQuery(id+"F0.wireOp",EDGE,"E8");var subQ1=sQuery(id+"F0.wireOp",EDGE,"E0.rect.right");Q1=makeQuery(id+"F3.boolean.opBoolean","SPLIT",EDGE,{"disambiguationData":[topologyDisambiguationEdgeConnected([makeQuery(id+"F1.opExtrude","SWEPT_FACE",FACE,{"disambiguationData":[OSD([subQ0])]})])],"derivedFrom":makeQuery(id+"F2.boolean.opBoolean","MERGE",EDGE,{"derivedFrom":[makeQuery(id+"F1.opExtrude","SWEPT_EDGE",EDGE,{"disambiguationData":[OSD([subQ1,subQ0])]}),makeQuery(id+"F2.opExtrude","SWEPT_EDGE",EDGE,{"disambiguationData":[OSD([subQ1,subQ0])]})]})});}
            var Q2;
            {var subQ0=sQuery(id+"F0.wireOp",EDGE,"E5");var subQ1=sQuery(id+"F0.wireOp",EDGE,"E0.rect.bottom");Q2=makeQuery(id+"F3.boolean.opBoolean","SPLIT",EDGE,{"disambiguationData":[topologyDisambiguationEdgeConnected([makeQuery(id+"F1.opExtrude","SWEPT_FACE",FACE,{"disambiguationData":[OSD([subQ0])]})])],"derivedFrom":makeQuery(id+"F2.boolean.opBoolean","MERGE",EDGE,{"derivedFrom":[makeQuery(id+"F1.opExtrude","SWEPT_EDGE",EDGE,{"disambiguationData":[OSD([subQ1,subQ0])]}),makeQuery(id+"F2.opExtrude","SWEPT_EDGE",EDGE,{"disambiguationData":[OSD([subQ1,subQ0])]})]})});}
            var Q3;
            {var subQ0=sQuery(id+"F0.wireOp",EDGE,"E5");var subQ1=sQuery(id+"F0.wireOp",EDGE,"E0.rect.left");Q3=makeQuery(id+"F3.boolean.opBoolean","SPLIT",EDGE,{"disambiguationData":[topologyDisambiguationEdgeConnected([makeQuery(id+"F1.opExtrude","SWEPT_FACE",FACE,{"disambiguationData":[OSD([subQ0])]})])],"derivedFrom":makeQuery(id+"F2.boolean.opBoolean","MERGE",EDGE,{"derivedFrom":[makeQuery(id+"F1.opExtrude","SWEPT_EDGE",EDGE,{"disambiguationData":[OSD([subQ1,subQ0])]}),makeQuery(id+"F2.opExtrude","SWEPT_EDGE",EDGE,{"disambiguationData":[OSD([subQ1,subQ0])]})]})});}
            var Q4;
            {var subQ0=sQuery(id+"F0.wireOp",EDGE,"E0.rect.top");var subQ1=sQuery(id+"F0.wireOp",EDGE,"E10");Q4=makeQuery(id+"F3.boolean.opBoolean","SPLIT",EDGE,{"disambiguationData":[topologyDisambiguationEdgeConnected([makeQuery(id+"F1.opExtrude","SWEPT_FACE",FACE,{"disambiguationData":[OSD([subQ1])]})])],"derivedFrom":makeQuery(id+"F2.boolean.opBoolean","MERGE",EDGE,{"derivedFrom":[makeQuery(id+"F1.opExtrude","SWEPT_EDGE",EDGE,{"disambiguationData":[OSD([subQ0,subQ1])]}),makeQuery(id+"F2.opExtrude","SWEPT_EDGE",EDGE,{"disambiguationData":[OSD([subQ0,subQ1])]})]})});}
            var Q5;
            {var subQ0=sQuery(id+"F0.wireOp",EDGE,"E0.rect.right");var subQ1=sQuery(id+"F0.wireOp",EDGE,"E10");Q5=makeQuery(id+"F3.boolean.opBoolean","SPLIT",EDGE,{"disambiguationData":[topologyDisambiguationEdgeConnected([makeQuery(id+"F1.opExtrude","SWEPT_FACE",FACE,{"disambiguationData":[OSD([subQ1])]})])],"derivedFrom":makeQuery(id+"F2.boolean.opBoolean","MERGE",EDGE,{"derivedFrom":[makeQuery(id+"F1.opExtrude","SWEPT_EDGE",EDGE,{"disambiguationData":[OSD([subQ0,subQ1])]}),makeQuery(id+"F2.opExtrude","SWEPT_EDGE",EDGE,{"disambiguationData":[OSD([subQ0,subQ1])]})]})});}
            var Q6;
            {var subQ0=sQuery(id+"F0.wireOp",EDGE,"E0.rect.left");var subQ1=sQuery(id+"F0.wireOp",EDGE,"E12");Q6=makeQuery(id+"F3.boolean.opBoolean","SPLIT",EDGE,{"disambiguationData":[topologyDisambiguationEdgeConnected([makeQuery(id+"F1.opExtrude","SWEPT_FACE",FACE,{"disambiguationData":[OSD([subQ1])]})])],"derivedFrom":makeQuery(id+"F2.boolean.opBoolean","MERGE",EDGE,{"derivedFrom":[makeQuery(id+"F1.opExtrude","SWEPT_EDGE",EDGE,{"disambiguationData":[OSD([subQ0,subQ1])]}),makeQuery(id+"F2.opExtrude","SWEPT_EDGE",EDGE,{"disambiguationData":[OSD([subQ0,subQ1])]})]})});}
            var Q7;
            {var subQ0=sQuery(id+"F0.wireOp",EDGE,"E12");var subQ1=sQuery(id+"F0.wireOp",EDGE,"E0.rect.top");Q7=makeQuery(id+"F3.boolean.opBoolean","SPLIT",EDGE,{"disambiguationData":[topologyDisambiguationEdgeConnected([makeQuery(id+"F1.opExtrude","SWEPT_FACE",FACE,{"disambiguationData":[OSD([subQ0])]})])],"derivedFrom":makeQuery(id+"F2.boolean.opBoolean","MERGE",EDGE,{"derivedFrom":[makeQuery(id+"F1.opExtrude","SWEPT_EDGE",EDGE,{"disambiguationData":[OSD([subQ1,subQ0])]}),makeQuery(id+"F2.opExtrude","SWEPT_EDGE",EDGE,{"disambiguationData":[OSD([subQ1,subQ0])]})]})});}
            chamfer(context, id + "F5", {"entities" : qUnion([Q0, Q1, Q2, Q3, Q4, Q5, Q6, Q7]), "width" : .9 * mm, "tangentPropagation" : true});
        }
        {
            var Q0;
            {var subQ0=sQuery(id+"F0.wireOp",EDGE,"E6");Q0=makeQuery(id+"F2.boolean.opBoolean","INTERSECT",EDGE,{"disambiguationData":[OD(0.0)],"derivedFrom":[makeQuery(id+"F1.opExtrude","CAP_FACE",FACE,{"disambiguationData":[OSD([sQuery(id+"F0.wireOp",EDGE,"E0.rect.bottom"),sQuery(id+"F0.wireOp",EDGE,"E0.rect.top"),sQuery(id+"F0.wireOp",EDGE,"E0.rect.left"),sQuery(id+"F0.wireOp",EDGE,"E0.rect.right"),sQuery(id+"F0.wireOp",EDGE,"E5"),subQ0,sQuery(id+"F0.wireOp",EDGE,"E8"),sQuery(id+"F0.wireOp",EDGE,"E9"),sQuery(id+"F0.wireOp",EDGE,"E10"),sQuery(id+"F0.wireOp",EDGE,"E11"),sQuery(id+"F0.wireOp",EDGE,"E12"),sQuery(id+"F0.wireOp",EDGE,"E13"),sQuery(id+"F0.wireOp",EDGE,"E14"),sQuery(id+"F0.wireOp",EDGE,"E15"),sQuery(id+"F0.wireOp",EDGE,"E16"),sQuery(id+"F0.wireOp",EDGE,"E17"),sQuery(id+"F0.wireOp",EDGE,"E18"),sQuery(id+"F0.wireOp",EDGE,"E19"),sQuery(id+"F0.wireOp",EDGE,"E20"),sQuery(id+"F0.wireOp",EDGE,"E21"),sQuery(id+"F0.wireOp",EDGE,"E23"),sQuery(id+"F0.wireOp",EDGE,"E24"),sQuery(id+"F0.wireOp",EDGE,"E26"),sQuery(id+"F0.wireOp",EDGE,"E27"),sQuery(id+"F0.wireOp",EDGE,"E28"),sQuery(id+"F0.wireOp",EDGE,"E29"),sQuery(id+"F0.wireOp",EDGE,"E30"),sQuery(id+"F0.wireOp",EDGE,"E31"),sQuery(id+"F0.wireOp",EDGE,"E32"),sQuery(id+"F0.wireOp",EDGE,"E33"),sQuery(id+"F0.wireOp",EDGE,"E35"),sQuery(id+"F0.wireOp",EDGE,"E36"),sQuery(id+"F0.wireOp",EDGE,"E37"),sQuery(id+"F0.wireOp",EDGE,"E38"),sQuery(id+"F0.wireOp",EDGE,"E39"),sQuery(id+"F0.wireOp",EDGE,"E40")])],"isStart":false}),makeQuery(id+"F2.opExtrude","SWEPT_FACE",FACE,{"disambiguationData":[OSD([subQ0])]})]});}
            var Q1;
            {var subQ0=sQuery(id+"F0.wireOp",EDGE,"E6");Q1=makeQuery(id+"F2.boolean.opBoolean","INTERSECT",EDGE,{"disambiguationData":[OD(1.0)],"derivedFrom":[makeQuery(id+"F1.opExtrude","CAP_FACE",FACE,{"disambiguationData":[OSD([sQuery(id+"F0.wireOp",EDGE,"E0.rect.bottom"),sQuery(id+"F0.wireOp",EDGE,"E0.rect.top"),sQuery(id+"F0.wireOp",EDGE,"E0.rect.left"),sQuery(id+"F0.wireOp",EDGE,"E0.rect.right"),sQuery(id+"F0.wireOp",EDGE,"E5"),subQ0,sQuery(id+"F0.wireOp",EDGE,"E8"),sQuery(id+"F0.wireOp",EDGE,"E9"),sQuery(id+"F0.wireOp",EDGE,"E10"),sQuery(id+"F0.wireOp",EDGE,"E11"),sQuery(id+"F0.wireOp",EDGE,"E12"),sQuery(id+"F0.wireOp",EDGE,"E13"),sQuery(id+"F0.wireOp",EDGE,"E14"),sQuery(id+"F0.wireOp",EDGE,"E15"),sQuery(id+"F0.wireOp",EDGE,"E16"),sQuery(id+"F0.wireOp",EDGE,"E17"),sQuery(id+"F0.wireOp",EDGE,"E18"),sQuery(id+"F0.wireOp",EDGE,"E19"),sQuery(id+"F0.wireOp",EDGE,"E20"),sQuery(id+"F0.wireOp",EDGE,"E21"),sQuery(id+"F0.wireOp",EDGE,"E23"),sQuery(id+"F0.wireOp",EDGE,"E24"),sQuery(id+"F0.wireOp",EDGE,"E26"),sQuery(id+"F0.wireOp",EDGE,"E27"),sQuery(id+"F0.wireOp",EDGE,"E28"),sQuery(id+"F0.wireOp",EDGE,"E29"),sQuery(id+"F0.wireOp",EDGE,"E30"),sQuery(id+"F0.wireOp",EDGE,"E31"),sQuery(id+"F0.wireOp",EDGE,"E32"),sQuery(id+"F0.wireOp",EDGE,"E33"),sQuery(id+"F0.wireOp",EDGE,"E35"),sQuery(id+"F0.wireOp",EDGE,"E36"),sQuery(id+"F0.wireOp",EDGE,"E37"),sQuery(id+"F0.wireOp",EDGE,"E38"),sQuery(id+"F0.wireOp",EDGE,"E39"),sQuery(id+"F0.wireOp",EDGE,"E40")])],"isStart":false}),makeQuery(id+"F2.opExtrude","SWEPT_FACE",FACE,{"disambiguationData":[OSD([subQ0])]})]});}
            var Q2;
            {var subQ0=sQuery(id+"F0.wireOp",EDGE,"E9");Q2=makeQuery(id+"F2.boolean.opBoolean","INTERSECT",EDGE,{"disambiguationData":[OD(1.0)],"derivedFrom":[makeQuery(id+"F1.opExtrude","CAP_FACE",FACE,{"disambiguationData":[OSD([sQuery(id+"F0.wireOp",EDGE,"E0.rect.bottom"),sQuery(id+"F0.wireOp",EDGE,"E0.rect.top"),sQuery(id+"F0.wireOp",EDGE,"E0.rect.left"),sQuery(id+"F0.wireOp",EDGE,"E0.rect.right"),sQuery(id+"F0.wireOp",EDGE,"E5"),sQuery(id+"F0.wireOp",EDGE,"E6"),sQuery(id+"F0.wireOp",EDGE,"E8"),subQ0,sQuery(id+"F0.wireOp",EDGE,"E10"),sQuery(id+"F0.wireOp",EDGE,"E11"),sQuery(id+"F0.wireOp",EDGE,"E12"),sQuery(id+"F0.wireOp",EDGE,"E13"),sQuery(id+"F0.wireOp",EDGE,"E14"),sQuery(id+"F0.wireOp",EDGE,"E15"),sQuery(id+"F0.wireOp",EDGE,"E16"),sQuery(id+"F0.wireOp",EDGE,"E17"),sQuery(id+"F0.wireOp",EDGE,"E18"),sQuery(id+"F0.wireOp",EDGE,"E19"),sQuery(id+"F0.wireOp",EDGE,"E20"),sQuery(id+"F0.wireOp",EDGE,"E21"),sQuery(id+"F0.wireOp",EDGE,"E23"),sQuery(id+"F0.wireOp",EDGE,"E24"),sQuery(id+"F0.wireOp",EDGE,"E26"),sQuery(id+"F0.wireOp",EDGE,"E27"),sQuery(id+"F0.wireOp",EDGE,"E28"),sQuery(id+"F0.wireOp",EDGE,"E29"),sQuery(id+"F0.wireOp",EDGE,"E30"),sQuery(id+"F0.wireOp",EDGE,"E31"),sQuery(id+"F0.wireOp",EDGE,"E32"),sQuery(id+"F0.wireOp",EDGE,"E33"),sQuery(id+"F0.wireOp",EDGE,"E35"),sQuery(id+"F0.wireOp",EDGE,"E36"),sQuery(id+"F0.wireOp",EDGE,"E37"),sQuery(id+"F0.wireOp",EDGE,"E38"),sQuery(id+"F0.wireOp",EDGE,"E39"),sQuery(id+"F0.wireOp",EDGE,"E40")])],"isStart":false}),makeQuery(id+"F2.opExtrude","SWEPT_FACE",FACE,{"disambiguationData":[OSD([subQ0])]})]});}
            var Q3;
            {var subQ0=sQuery(id+"F0.wireOp",EDGE,"E9");Q3=makeQuery(id+"F2.boolean.opBoolean","INTERSECT",EDGE,{"disambiguationData":[OD(0.0)],"derivedFrom":[makeQuery(id+"F1.opExtrude","CAP_FACE",FACE,{"disambiguationData":[OSD([sQuery(id+"F0.wireOp",EDGE,"E0.rect.bottom"),sQuery(id+"F0.wireOp",EDGE,"E0.rect.top"),sQuery(id+"F0.wireOp",EDGE,"E0.rect.left"),sQuery(id+"F0.wireOp",EDGE,"E0.rect.right"),sQuery(id+"F0.wireOp",EDGE,"E5"),sQuery(id+"F0.wireOp",EDGE,"E6"),sQuery(id+"F0.wireOp",EDGE,"E8"),subQ0,sQuery(id+"F0.wireOp",EDGE,"E10"),sQuery(id+"F0.wireOp",EDGE,"E11"),sQuery(id+"F0.wireOp",EDGE,"E12"),sQuery(id+"F0.wireOp",EDGE,"E13"),sQuery(id+"F0.wireOp",EDGE,"E14"),sQuery(id+"F0.wireOp",EDGE,"E15"),sQuery(id+"F0.wireOp",EDGE,"E16"),sQuery(id+"F0.wireOp",EDGE,"E17"),sQuery(id+"F0.wireOp",EDGE,"E18"),sQuery(id+"F0.wireOp",EDGE,"E19"),sQuery(id+"F0.wireOp",EDGE,"E20"),sQuery(id+"F0.wireOp",EDGE,"E21"),sQuery(id+"F0.wireOp",EDGE,"E23"),sQuery(id+"F0.wireOp",EDGE,"E24"),sQuery(id+"F0.wireOp",EDGE,"E26"),sQuery(id+"F0.wireOp",EDGE,"E27"),sQuery(id+"F0.wireOp",EDGE,"E28"),sQuery(id+"F0.wireOp",EDGE,"E29"),sQuery(id+"F0.wireOp",EDGE,"E30"),sQuery(id+"F0.wireOp",EDGE,"E31"),sQuery(id+"F0.wireOp",EDGE,"E32"),sQuery(id+"F0.wireOp",EDGE,"E33"),sQuery(id+"F0.wireOp",EDGE,"E35"),sQuery(id+"F0.wireOp",EDGE,"E36"),sQuery(id+"F0.wireOp",EDGE,"E37"),sQuery(id+"F0.wireOp",EDGE,"E38"),sQuery(id+"F0.wireOp",EDGE,"E39"),sQuery(id+"F0.wireOp",EDGE,"E40")])],"isStart":false}),makeQuery(id+"F2.opExtrude","SWEPT_FACE",FACE,{"disambiguationData":[OSD([subQ0])]})]});}
            var Q4;
            {var subQ0=sQuery(id+"F0.wireOp",EDGE,"E11");Q4=makeQuery(id+"F2.boolean.opBoolean","INTERSECT",EDGE,{"disambiguationData":[OD(1.0)],"derivedFrom":[makeQuery(id+"F1.opExtrude","CAP_FACE",FACE,{"disambiguationData":[OSD([sQuery(id+"F0.wireOp",EDGE,"E0.rect.bottom"),sQuery(id+"F0.wireOp",EDGE,"E0.rect.top"),sQuery(id+"F0.wireOp",EDGE,"E0.rect.left"),sQuery(id+"F0.wireOp",EDGE,"E0.rect.right"),sQuery(id+"F0.wireOp",EDGE,"E5"),sQuery(id+"F0.wireOp",EDGE,"E6"),sQuery(id+"F0.wireOp",EDGE,"E8"),sQuery(id+"F0.wireOp",EDGE,"E9"),sQuery(id+"F0.wireOp",EDGE,"E10"),subQ0,sQuery(id+"F0.wireOp",EDGE,"E12"),sQuery(id+"F0.wireOp",EDGE,"E13"),sQuery(id+"F0.wireOp",EDGE,"E14"),sQuery(id+"F0.wireOp",EDGE,"E15"),sQuery(id+"F0.wireOp",EDGE,"E16"),sQuery(id+"F0.wireOp",EDGE,"E17"),sQuery(id+"F0.wireOp",EDGE,"E18"),sQuery(id+"F0.wireOp",EDGE,"E19"),sQuery(id+"F0.wireOp",EDGE,"E20"),sQuery(id+"F0.wireOp",EDGE,"E21"),sQuery(id+"F0.wireOp",EDGE,"E23"),sQuery(id+"F0.wireOp",EDGE,"E24"),sQuery(id+"F0.wireOp",EDGE,"E26"),sQuery(id+"F0.wireOp",EDGE,"E27"),sQuery(id+"F0.wireOp",EDGE,"E28"),sQuery(id+"F0.wireOp",EDGE,"E29"),sQuery(id+"F0.wireOp",EDGE,"E30"),sQuery(id+"F0.wireOp",EDGE,"E31"),sQuery(id+"F0.wireOp",EDGE,"E32"),sQuery(id+"F0.wireOp",EDGE,"E33"),sQuery(id+"F0.wireOp",EDGE,"E35"),sQuery(id+"F0.wireOp",EDGE,"E36"),sQuery(id+"F0.wireOp",EDGE,"E37"),sQuery(id+"F0.wireOp",EDGE,"E38"),sQuery(id+"F0.wireOp",EDGE,"E39"),sQuery(id+"F0.wireOp",EDGE,"E40")])],"isStart":false}),makeQuery(id+"F2.opExtrude","SWEPT_FACE",FACE,{"disambiguationData":[OSD([subQ0])]})]});}
            var Q5;
            {var subQ0=sQuery(id+"F0.wireOp",EDGE,"E11");Q5=makeQuery(id+"F2.boolean.opBoolean","INTERSECT",EDGE,{"disambiguationData":[OD(0.0)],"derivedFrom":[makeQuery(id+"F1.opExtrude","CAP_FACE",FACE,{"disambiguationData":[OSD([sQuery(id+"F0.wireOp",EDGE,"E0.rect.bottom"),sQuery(id+"F0.wireOp",EDGE,"E0.rect.top"),sQuery(id+"F0.wireOp",EDGE,"E0.rect.left"),sQuery(id+"F0.wireOp",EDGE,"E0.rect.right"),sQuery(id+"F0.wireOp",EDGE,"E5"),sQuery(id+"F0.wireOp",EDGE,"E6"),sQuery(id+"F0.wireOp",EDGE,"E8"),sQuery(id+"F0.wireOp",EDGE,"E9"),sQuery(id+"F0.wireOp",EDGE,"E10"),subQ0,sQuery(id+"F0.wireOp",EDGE,"E12"),sQuery(id+"F0.wireOp",EDGE,"E13"),sQuery(id+"F0.wireOp",EDGE,"E14"),sQuery(id+"F0.wireOp",EDGE,"E15"),sQuery(id+"F0.wireOp",EDGE,"E16"),sQuery(id+"F0.wireOp",EDGE,"E17"),sQuery(id+"F0.wireOp",EDGE,"E18"),sQuery(id+"F0.wireOp",EDGE,"E19"),sQuery(id+"F0.wireOp",EDGE,"E20"),sQuery(id+"F0.wireOp",EDGE,"E21"),sQuery(id+"F0.wireOp",EDGE,"E23"),sQuery(id+"F0.wireOp",EDGE,"E24"),sQuery(id+"F0.wireOp",EDGE,"E26"),sQuery(id+"F0.wireOp",EDGE,"E27"),sQuery(id+"F0.wireOp",EDGE,"E28"),sQuery(id+"F0.wireOp",EDGE,"E29"),sQuery(id+"F0.wireOp",EDGE,"E30"),sQuery(id+"F0.wireOp",EDGE,"E31"),sQuery(id+"F0.wireOp",EDGE,"E32"),sQuery(id+"F0.wireOp",EDGE,"E33"),sQuery(id+"F0.wireOp",EDGE,"E35"),sQuery(id+"F0.wireOp",EDGE,"E36"),sQuery(id+"F0.wireOp",EDGE,"E37"),sQuery(id+"F0.wireOp",EDGE,"E38"),sQuery(id+"F0.wireOp",EDGE,"E39"),sQuery(id+"F0.wireOp",EDGE,"E40")])],"isStart":false}),makeQuery(id+"F2.opExtrude","SWEPT_FACE",FACE,{"disambiguationData":[OSD([subQ0])]})]});}
            var Q6;
            {var subQ0=sQuery(id+"F0.wireOp",EDGE,"E13");Q6=makeQuery(id+"F2.boolean.opBoolean","INTERSECT",EDGE,{"disambiguationData":[OD(1.0)],"derivedFrom":[makeQuery(id+"F1.opExtrude","CAP_FACE",FACE,{"disambiguationData":[OSD([sQuery(id+"F0.wireOp",EDGE,"E0.rect.bottom"),sQuery(id+"F0.wireOp",EDGE,"E0.rect.top"),sQuery(id+"F0.wireOp",EDGE,"E0.rect.left"),sQuery(id+"F0.wireOp",EDGE,"E0.rect.right"),sQuery(id+"F0.wireOp",EDGE,"E5"),sQuery(id+"F0.wireOp",EDGE,"E6"),sQuery(id+"F0.wireOp",EDGE,"E8"),sQuery(id+"F0.wireOp",EDGE,"E9"),sQuery(id+"F0.wireOp",EDGE,"E10"),sQuery(id+"F0.wireOp",EDGE,"E11"),sQuery(id+"F0.wireOp",EDGE,"E12"),subQ0,sQuery(id+"F0.wireOp",EDGE,"E14"),sQuery(id+"F0.wireOp",EDGE,"E15"),sQuery(id+"F0.wireOp",EDGE,"E16"),sQuery(id+"F0.wireOp",EDGE,"E17"),sQuery(id+"F0.wireOp",EDGE,"E18"),sQuery(id+"F0.wireOp",EDGE,"E19"),sQuery(id+"F0.wireOp",EDGE,"E20"),sQuery(id+"F0.wireOp",EDGE,"E21"),sQuery(id+"F0.wireOp",EDGE,"E23"),sQuery(id+"F0.wireOp",EDGE,"E24"),sQuery(id+"F0.wireOp",EDGE,"E26"),sQuery(id+"F0.wireOp",EDGE,"E27"),sQuery(id+"F0.wireOp",EDGE,"E28"),sQuery(id+"F0.wireOp",EDGE,"E29"),sQuery(id+"F0.wireOp",EDGE,"E30"),sQuery(id+"F0.wireOp",EDGE,"E31"),sQuery(id+"F0.wireOp",EDGE,"E32"),sQuery(id+"F0.wireOp",EDGE,"E33"),sQuery(id+"F0.wireOp",EDGE,"E35"),sQuery(id+"F0.wireOp",EDGE,"E36"),sQuery(id+"F0.wireOp",EDGE,"E37"),sQuery(id+"F0.wireOp",EDGE,"E38"),sQuery(id+"F0.wireOp",EDGE,"E39"),sQuery(id+"F0.wireOp",EDGE,"E40")])],"isStart":false}),makeQuery(id+"F2.opExtrude","SWEPT_FACE",FACE,{"disambiguationData":[OSD([subQ0])]})]});}
            var Q7;
            {var subQ0=sQuery(id+"F0.wireOp",EDGE,"E13");Q7=makeQuery(id+"F2.boolean.opBoolean","INTERSECT",EDGE,{"disambiguationData":[OD(0.0)],"derivedFrom":[makeQuery(id+"F1.opExtrude","CAP_FACE",FACE,{"disambiguationData":[OSD([sQuery(id+"F0.wireOp",EDGE,"E0.rect.bottom"),sQuery(id+"F0.wireOp",EDGE,"E0.rect.top"),sQuery(id+"F0.wireOp",EDGE,"E0.rect.left"),sQuery(id+"F0.wireOp",EDGE,"E0.rect.right"),sQuery(id+"F0.wireOp",EDGE,"E5"),sQuery(id+"F0.wireOp",EDGE,"E6"),sQuery(id+"F0.wireOp",EDGE,"E8"),sQuery(id+"F0.wireOp",EDGE,"E9"),sQuery(id+"F0.wireOp",EDGE,"E10"),sQuery(id+"F0.wireOp",EDGE,"E11"),sQuery(id+"F0.wireOp",EDGE,"E12"),subQ0,sQuery(id+"F0.wireOp",EDGE,"E14"),sQuery(id+"F0.wireOp",EDGE,"E15"),sQuery(id+"F0.wireOp",EDGE,"E16"),sQuery(id+"F0.wireOp",EDGE,"E17"),sQuery(id+"F0.wireOp",EDGE,"E18"),sQuery(id+"F0.wireOp",EDGE,"E19"),sQuery(id+"F0.wireOp",EDGE,"E20"),sQuery(id+"F0.wireOp",EDGE,"E21"),sQuery(id+"F0.wireOp",EDGE,"E23"),sQuery(id+"F0.wireOp",EDGE,"E24"),sQuery(id+"F0.wireOp",EDGE,"E26"),sQuery(id+"F0.wireOp",EDGE,"E27"),sQuery(id+"F0.wireOp",EDGE,"E28"),sQuery(id+"F0.wireOp",EDGE,"E29"),sQuery(id+"F0.wireOp",EDGE,"E30"),sQuery(id+"F0.wireOp",EDGE,"E31"),sQuery(id+"F0.wireOp",EDGE,"E32"),sQuery(id+"F0.wireOp",EDGE,"E33"),sQuery(id+"F0.wireOp",EDGE,"E35"),sQuery(id+"F0.wireOp",EDGE,"E36"),sQuery(id+"F0.wireOp",EDGE,"E37"),sQuery(id+"F0.wireOp",EDGE,"E38"),sQuery(id+"F0.wireOp",EDGE,"E39"),sQuery(id+"F0.wireOp",EDGE,"E40")])],"isStart":false}),makeQuery(id+"F2.opExtrude","SWEPT_FACE",FACE,{"disambiguationData":[OSD([subQ0])]})]});}
            fillet(context, id + "F6", {"entities" : qUnion([Q0, Q1, Q2, Q3, Q4, Q5, Q6, Q7]), "radius" : 6 * mm, "tangentPropagation" : true, "allowEdgeOverflow" : false});
        }
    });
